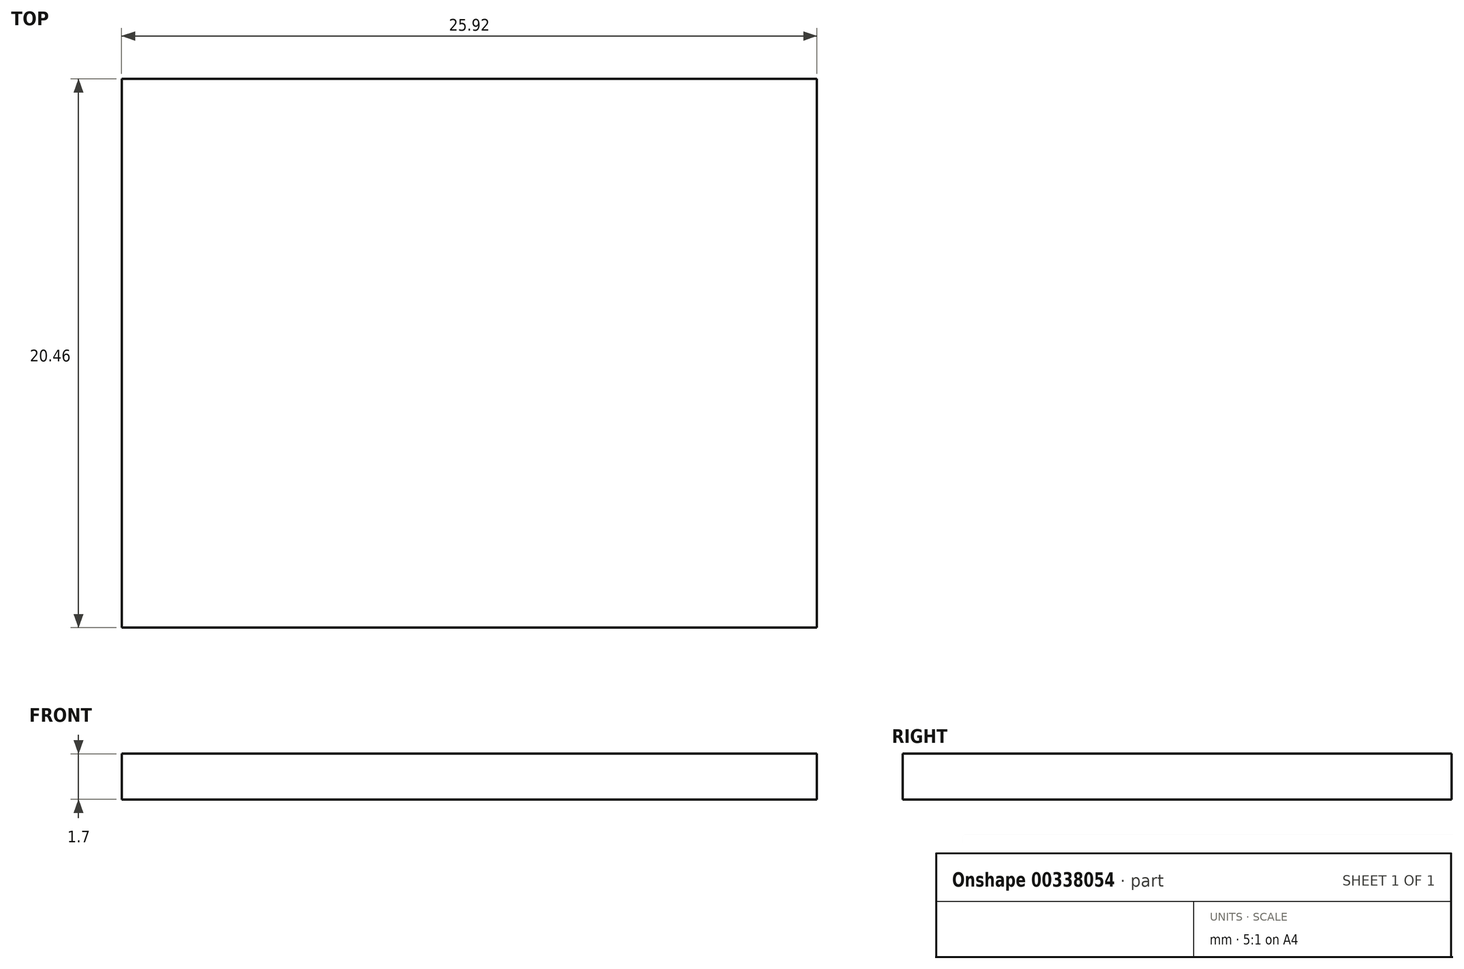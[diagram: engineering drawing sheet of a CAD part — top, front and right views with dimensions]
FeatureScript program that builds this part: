
annotation { "Feature Type Name" : "Feature", "Feature Type Description" : "" }
export const myFeature = defineFeature(function(context is Context, id is Id, definition is map)
    precondition{}
    {
        {
            var Q0;
            Q0=qCreatedBy(makeId("Top.planeOp"),FACE);
            var sketch = newSketch(context, id + "F0", { "sketchPlane" : qUnion([Q0])});
            skLineSegment(sketch, "E0.bottom", {"start": v(12.96, -10.23) * mm, "end": v(-12.96, -10.23) * mm});
            skLineSegment(sketch, "E0.top", {"start": v(12.96, 10.23) * mm, "end": v(-12.96, 10.23) * mm});
            skLineSegment(sketch, "E0.left", {"start": v(12.96, -10.23) * mm, "end": v(12.96, 10.23) * mm});
            skLineSegment(sketch, "E0.right", {"start": v(-12.96, -10.23) * mm, "end": v(-12.95, 10.23) * mm});
            skPoint(sketch, "E0.middle", {"position": v(0, 0) * mm});
            skSolve(sketch);
        }
        {
            var Q0;
            Q0=qSketchRegion(id+"F0",true);
            extrude(context, id + "F1", {"entities" : qUnion([Q0]), "endBound" : BoundingType.SYMMETRIC, "depth" : 1.71 * mm});
        }
    });
